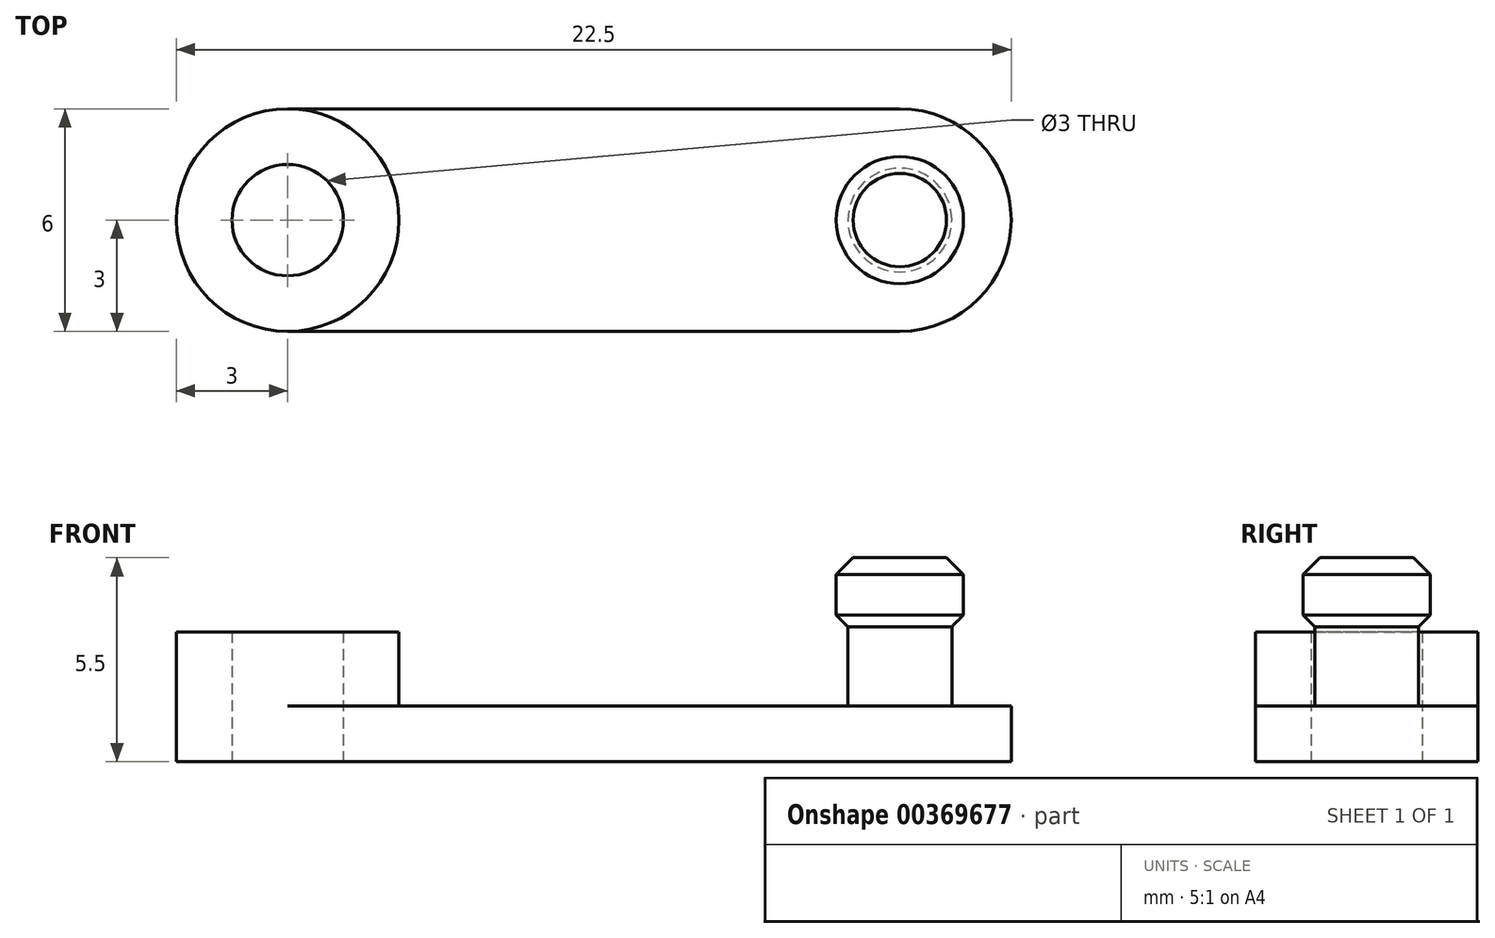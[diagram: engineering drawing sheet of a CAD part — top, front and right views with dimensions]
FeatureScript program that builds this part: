
annotation { "Feature Type Name" : "Feature", "Feature Type Description" : "" }
export const myFeature = defineFeature(function(context is Context, id is Id, definition is map)
    precondition{}
    {
        {
            var Q0;
            Q0=qCreatedBy(makeId("Top.planeOp"),FACE);
            var sketch = newSketch(context, id + "F0", { "sketchPlane" : qUnion([Q0])});
            skLineSegment(sketch, "E0.bottom", {"start": v(9.5, -3) * mm, "end": v(-9.5, -3) * mm});
            skLineSegment(sketch, "E0.top", {"start": v(9.5, 3) * mm, "end": v(-9.5, 3) * mm});
            skLineSegment(sketch, "E0.right", {"start": v(-9.5, -3) * mm, "end": v(-9.5, 3) * mm});
            skPoint(sketch, "E0.middle", {"position": v(0, 0) * mm});
            skCircle(sketch, "E1", {"center": v(-9.5, 0) * mm, "radius": 3 * mm});
            skCircle(sketch, "E2", {"center": v(7, 0) * mm, "radius": 3 * mm});
            skCircle(sketch, "E3", {"center": v(-9.5, 0) * mm, "radius": 1.5 * mm});
            skSolve(sketch);
        }
        {
            var Q0;
            Q0 = qSketchRegion(id + "F0", true);
            extrude(context, id + "F1", {"entities" : qUnion([Q0]), "depth" : 1.5 * mm, "offsetDistance" : 25.4 * mm});
        }
        {
            var Q0;
            Q0=makeQuery(id+"F1.opExtrude","CAP_FACE",FACE,{"disambiguationData":[OSD([sQuery(id+"F0.wireOp",EDGE,"E0.bottom"),sQuery(id+"F0.wireOp",EDGE,"E0.top"),sQuery(id+"F0.wireOp",EDGE,"E1"),sQuery(id+"F0.wireOp",EDGE,"E2"),sQuery(id+"F0.wireOp",EDGE,"E3")])],"isStart":false});
            var sketch = newSketch(context, id + "F2", { "sketchPlane" : qUnion([Q0])});
            skCircle(sketch, "E4", {"center": v(7, 0) * mm, "radius": 1.4 * mm});
            skSolve(sketch);
        }
        {
            var Q0;
            Q0 = qSketchRegion(id + "F2", true);
            extrude(context, id + "F3", {"entities" : qUnion([Q0]), "operationType" : NewBodyOperationType.ADD, "depth" : 4 * mm, "offsetDistance" : 25.4 * mm});
        }
        {
            var Q0;
            Q0=makeQuery(id+"F3.opExtrude","CAP_FACE",FACE,{"disambiguationData":[OSD([sQuery(id+"F2.wireOp",EDGE,"E4")])],"isStart":false});
            var sketch = newSketch(context, id + "F4", { "sketchPlane" : qUnion([Q0])});
            skCircle(sketch, "E5", {"center": v(7, 0) * mm, "radius": 1.71 * mm});
            skSolve(sketch);
        }
        {
            var Q0;
            Q0 = qSketchRegion(id + "F4", true);
            extrude(context, id + "F5", {"entities" : qUnion([Q0]), "operationType" : NewBodyOperationType.ADD, "oppositeDirection" : true, "depth" : 2 * mm, "offsetDistance" : 25.4 * mm});
        }
        {
            var Q0;
            Q0=makeQuery(id+"F5.opExtrude","CAP_EDGE",EDGE,{"disambiguationData":[OSD([sQuery(id+"F4.wireOp",EDGE,"E5")])],"isStart":true});
            chamfer(context, id + "F6", {"entities" : qUnion([Q0]), "width" : 0.46 * mm, "tangentPropagation" : true});
        }
        {
            var Q0;
            Q0=makeQuery(id+"F5.opExtrude","CAP_EDGE",EDGE,{"disambiguationData":[OSD([sQuery(id+"F4.wireOp",EDGE,"E5")])],"isStart":false});
            chamfer(context, id + "F7", {"entities" : qUnion([Q0]), "width" : 0.46 * mm, "tangentPropagation" : true});
        }
        {
            var Q0;
            Q0=makeQuery(id+"F1.opExtrude","CAP_FACE",FACE,{"disambiguationData":[OSD([sQuery(id+"F0.wireOp",EDGE,"E0.bottom"),sQuery(id+"F0.wireOp",EDGE,"E0.top"),sQuery(id+"F0.wireOp",EDGE,"E1"),sQuery(id+"F0.wireOp",EDGE,"E2"),sQuery(id+"F0.wireOp",EDGE,"E3")])],"isStart":false});
            var sketch = newSketch(context, id + "F8", { "sketchPlane" : qUnion([Q0])});
            skCircle(sketch, "E6", {"center": v(-9.5, 0) * mm, "radius": 3 * mm});
            skSolve(sketch);
        }
        {
            var Q0;
            Q0 = qSketchRegion(id + "F8", true);
            extrude(context, id + "F9", {"entities" : qUnion([Q0]), "operationType" : NewBodyOperationType.ADD, "depth" : 2 * mm, "offsetDistance" : 25.4 * mm});
        }
        {
            var Q0;
            Q0=makeQuery(id+"F9.opExtrude","CAP_FACE",FACE,{"disambiguationData":[OSD([sQuery(id+"F8.wireOp",EDGE,"E6")])],"isStart":true});
            extrude(context, id + "F10", {"entities" : qUnion([Q0]), "operationType" : NewBodyOperationType.REMOVE, "oppositeDirection" : true, "depth" : 25.4 * mm, "offsetDistance" : 25.4 * mm});
        }
    });
